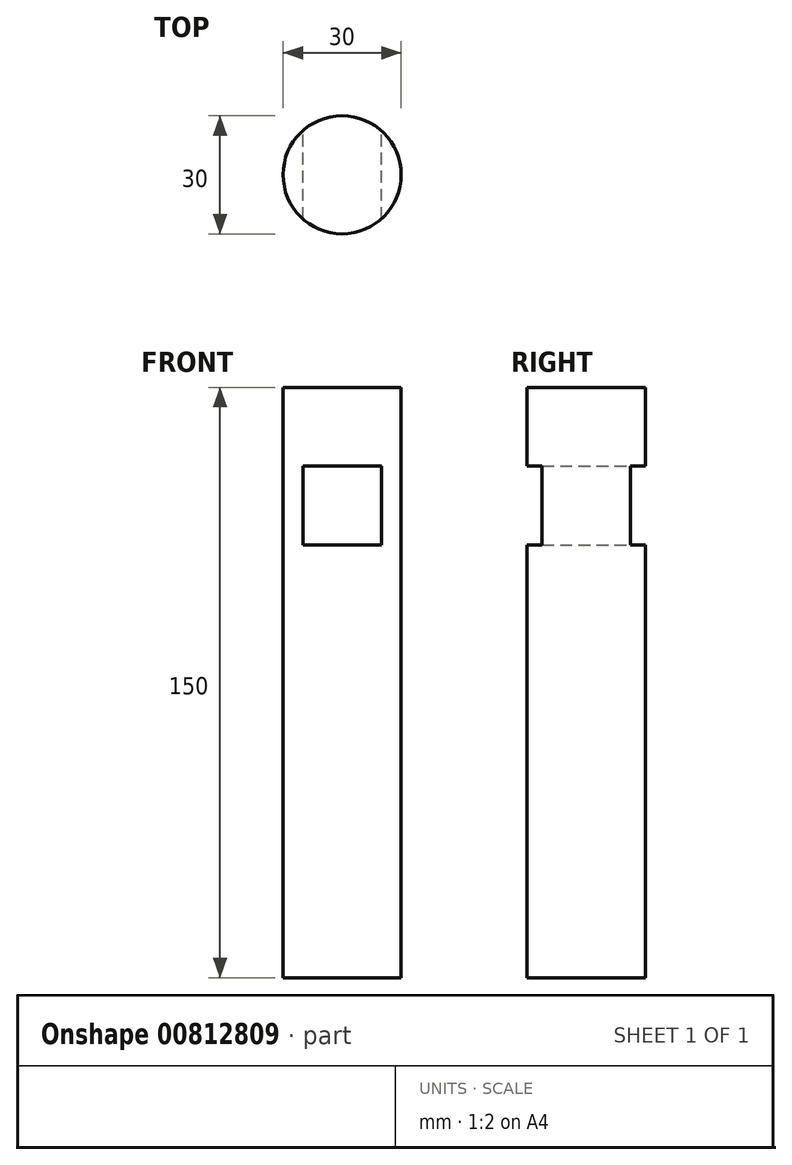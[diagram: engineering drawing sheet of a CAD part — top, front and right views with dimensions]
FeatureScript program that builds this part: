
annotation { "Feature Type Name" : "Feature", "Feature Type Description" : "" }
export const myFeature = defineFeature(function(context is Context, id is Id, definition is map)
    precondition{}
    {
        {
            var Q0;
            Q0=qCreatedBy(makeId("Top.planeOp"),FACE);
            var sketch = newSketch(context, id + "F0", { "sketchPlane" : qUnion([Q0])});
            skCircle(sketch, "E0", {"center": v(0, 0) * mm, "radius": 15 * mm});
            skSolve(sketch);
        }
        {
            var Q0;
            Q0 = qSketchRegion(id + "F0", true);
            extrude(context, id + "F1", {"entities" : qUnion([Q0]), "depth" : 150 * mm, "offsetDistance" : 25 * mm});
        }
        {
            var Q0;
            Q0=qCreatedBy(makeId("Front.planeOp"),FACE);
            var sketch = newSketch(context, id + "F2", { "sketchPlane" : qUnion([Q0])});
            skLineSegment(sketch, "E1.bottom", {"start": v(-10, 130) * mm, "end": v(10, 130) * mm});
            skLineSegment(sketch, "E1.top", {"start": v(-10, 110) * mm, "end": v(10, 110) * mm});
            skLineSegment(sketch, "E1.left", {"start": v(-10, 130) * mm, "end": v(-10, 110) * mm});
            skLineSegment(sketch, "E1.right", {"start": v(10, 130) * mm, "end": v(10, 110) * mm});
            skSolve(sketch);
        }
        {
            var Q0;
            Q0 = qSketchRegion(id + "F2", true);
            extrude(context, id + "F3", {"entities" : qUnion([Q0]), "operationType" : NewBodyOperationType.REMOVE, "endBound" : BoundingType.SYMMETRIC, "depth" : 200 * mm, "offsetDistance" : 25 * mm});
        }
    });
